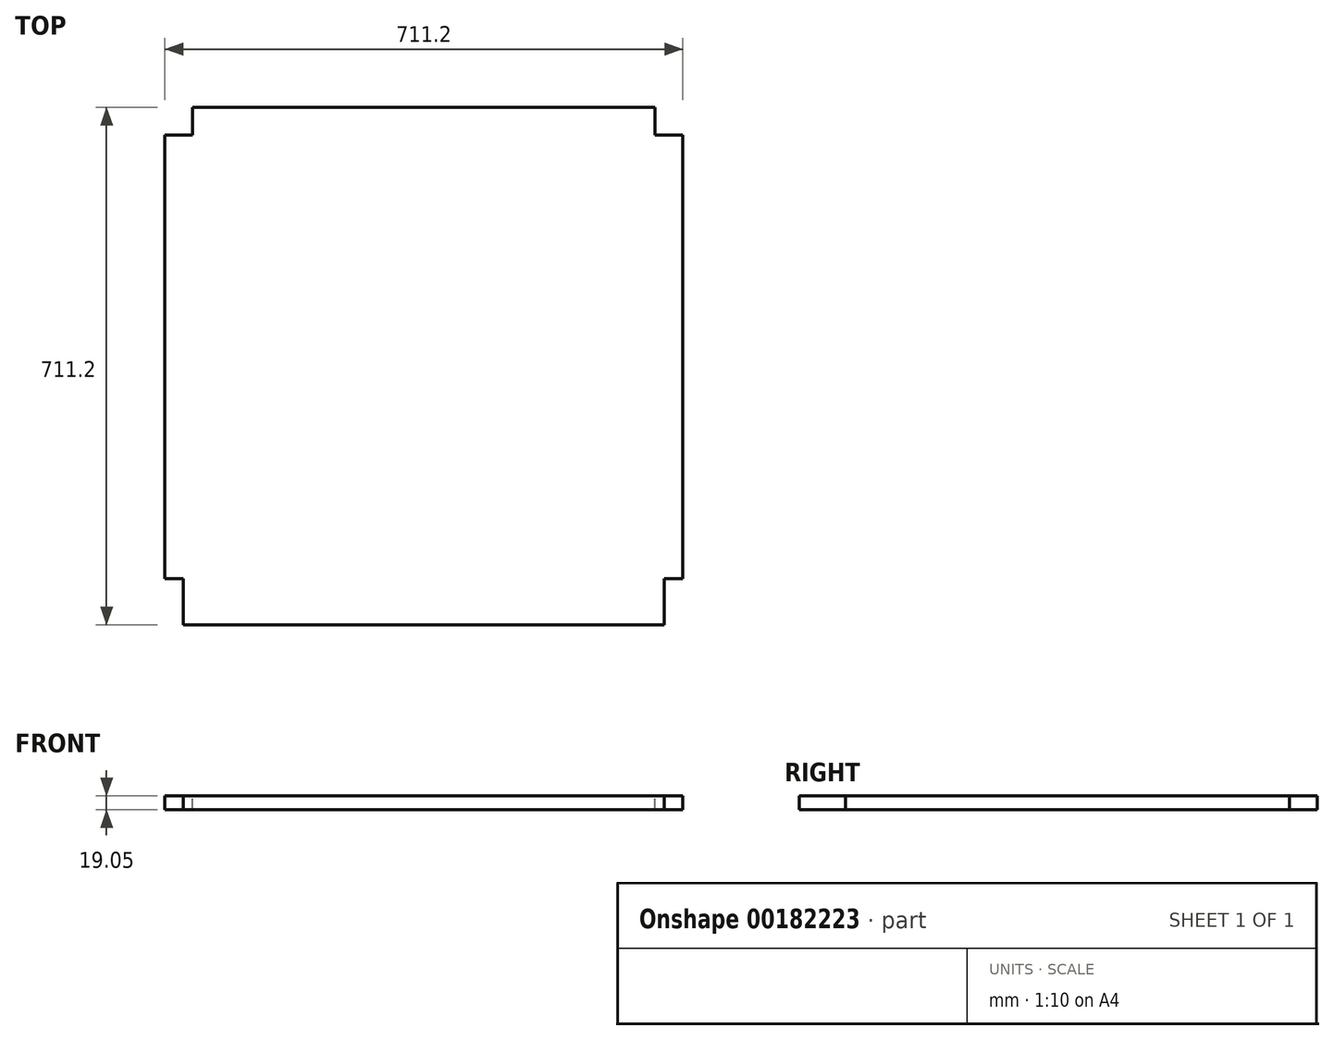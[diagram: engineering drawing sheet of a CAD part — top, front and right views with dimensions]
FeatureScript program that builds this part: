
annotation { "Feature Type Name" : "Feature", "Feature Type Description" : "" }
export const myFeature = defineFeature(function(context is Context, id is Id, definition is map)
    precondition{}
    {
        {
            var Q0;
            Q0=qCreatedBy(makeId("Top.planeOp"),FACE);
            var sketch = newSketch(context, id + "F0", { "sketchPlane" : qUnion([Q0])});
            skLineSegment(sketch, "E0.bottom", {"start": v(24.33, 7.29) * mm, "end": v(684.73, 7.29) * mm});
            skLineSegment(sketch, "E0.top", {"start": v(37.03, 718.49) * mm, "end": v(672.03, 718.49) * mm});
            skLineSegment(sketch, "E0.left", {"start": v(-1.07, 70.79) * mm, "end": v(-1.07, 680.39) * mm});
            skLineSegment(sketch, "E0.right", {"start": v(710.13, 70.79) * mm, "end": v(710.13, 680.39) * mm});
            skLineSegment(sketch, "E1.top", {"start": v(-1.07, 680.39) * mm, "end": v(37.03, 680.39) * mm});
            skLineSegment(sketch, "E1.right", {"start": v(37.03, 718.49) * mm, "end": v(37.03, 680.39) * mm});
            skLineSegment(sketch, "E2.top", {"start": v(710.13, 680.39) * mm, "end": v(672.03, 680.39) * mm});
            skLineSegment(sketch, "E2.right", {"start": v(672.03, 718.49) * mm, "end": v(672.03, 680.39) * mm});
            skLineSegment(sketch, "E3.top", {"start": v(-1.07, 70.79) * mm, "end": v(24.33, 70.79) * mm});
            skLineSegment(sketch, "E3.right", {"start": v(24.33, 7.29) * mm, "end": v(24.33, 70.79) * mm});
            skLineSegment(sketch, "E4.top", {"start": v(710.13, 70.79) * mm, "end": v(684.73, 70.79) * mm});
            skLineSegment(sketch, "E4.right", {"start": v(684.73, 7.29) * mm, "end": v(684.73, 70.79) * mm});
            skSolve(sketch);
        }
        {
            var Q0;
            Q0=qSketchRegion(id+"F0",true);
            extrude(context, id + "F1", {"entities" : qUnion([Q0]), "oppositeDirection" : true, "depth" : 19.05 * mm});
        }
    });
